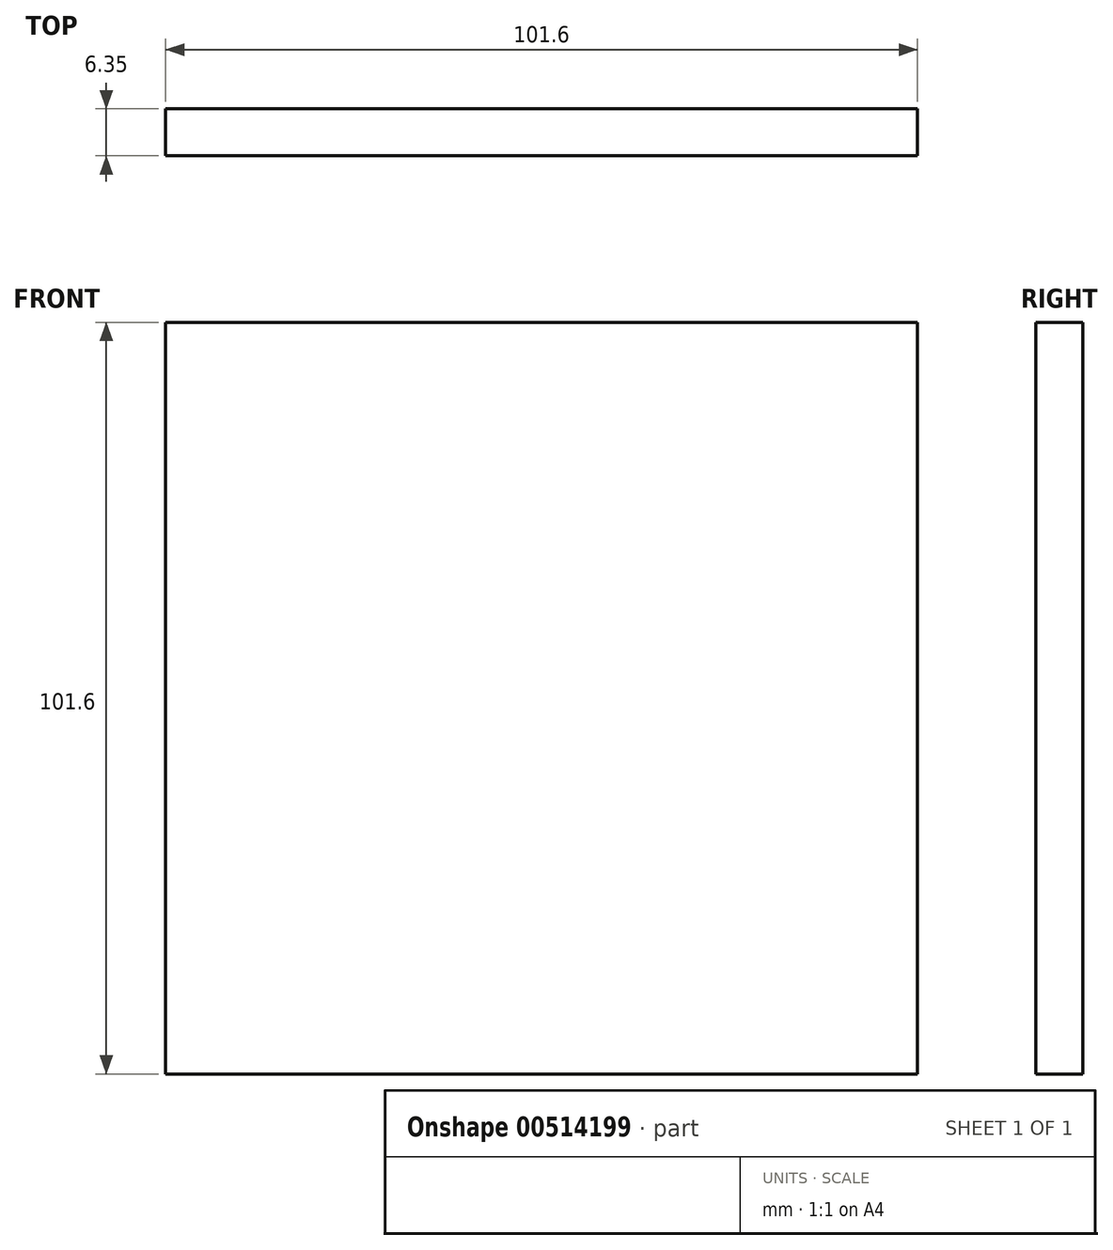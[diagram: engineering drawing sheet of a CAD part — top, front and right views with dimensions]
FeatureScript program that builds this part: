
annotation { "Feature Type Name" : "Feature", "Feature Type Description" : "" }
export const myFeature = defineFeature(function(context is Context, id is Id, definition is map)
    precondition{}
    {
        {
            var Q0;
            Q0=qCreatedBy(makeId("Front.planeOp"),FACE);
            var sketch = newSketch(context, id + "F0", { "sketchPlane" : qUnion([Q0])});
            skLineSegment(sketch, "E0.bottom", {"start": v(-58.66, 111.94) * mm, "end": v(42.94, 111.94) * mm});
            skLineSegment(sketch, "E0.top", {"start": v(-58.66, 10.34) * mm, "end": v(42.94, 10.34) * mm});
            skLineSegment(sketch, "E0.left", {"start": v(-58.66, 111.94) * mm, "end": v(-58.66, 10.34) * mm});
            skLineSegment(sketch, "E0.right", {"start": v(42.94, 111.94) * mm, "end": v(42.94, 10.34) * mm});
            skSolve(sketch);
        }
        {
            var Q0;
            Q0 = qSketchRegion(id + "F0", true);
            extrude(context, id + "F1", {"entities" : qUnion([Q0]), "depth" : 6.35 * mm, "offsetDistance" : 25.4 * mm});
        }
    });
